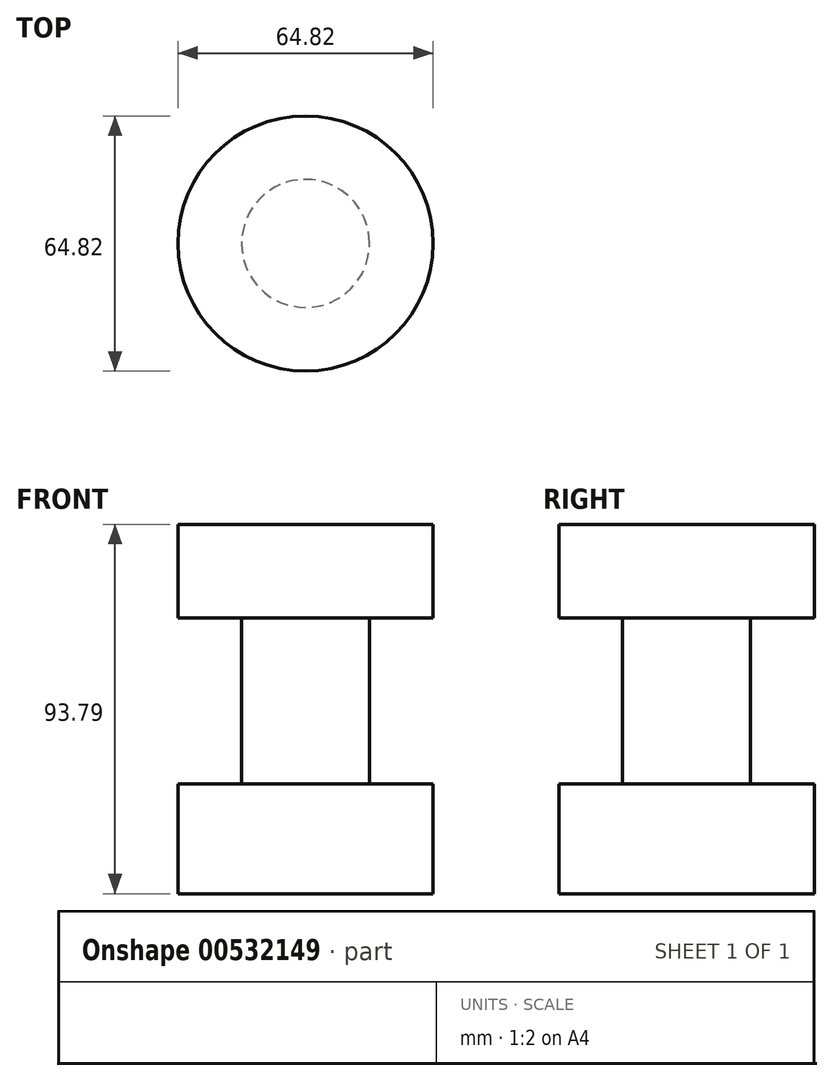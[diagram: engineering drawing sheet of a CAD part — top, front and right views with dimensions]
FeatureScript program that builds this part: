
annotation { "Feature Type Name" : "Feature", "Feature Type Description" : "" }
export const myFeature = defineFeature(function(context is Context, id is Id, definition is map)
    precondition{}
    {
        {
            var Q0;
            Q0=qCreatedBy(makeId("Front.planeOp"),FACE);
            var sketch = newSketch(context, id + "F0", { "sketchPlane" : qUnion([Q0])});
            skLineSegment(sketch, "E0.bottom", {"start": v(0, 0) * mm, "end": v(-32.4, 0) * mm});
            skLineSegment(sketch, "E0.top", {"start": v(0, 93.79) * mm, "end": v(-32.4, 93.79) * mm});
            skLineSegment(sketch, "E0.left", {"start": v(0, 0) * mm, "end": v(0, 93.79) * mm});
            skLineSegment(sketch, "E0.right", {"start": v(-32.4, 0) * mm, "end": v(-32.4, 93.79) * mm});
            skSolve(sketch);
        }
        {
            var Q0;
            Q0 = qSketchRegion(id + "F0", true);
            var Q1;
            Q1=sQuery(id+"F0.wireOp",EDGE,"E0.left");
            revolve(context, id + "F1", {"entities" : qUnion([Q0]), "axis" : qUnion([Q1]), "revolveType" : RevolveType.FULL});
        }
        {
            var Q0;
            Q0=qCreatedBy(makeId("Front.planeOp"),FACE);
            var sketch = newSketch(context, id + "F2", { "sketchPlane" : qUnion([Q0])});
            skLineSegment(sketch, "E1.bottom", {"start": v(-38.69, 70.04) * mm, "end": v(-16.26, 70.04) * mm});
            skLineSegment(sketch, "E1.top", {"start": v(-38.69, 27.94) * mm, "end": v(-16.26, 27.94) * mm});
            skLineSegment(sketch, "E1.left", {"start": v(-38.69, 70.04) * mm, "end": v(-38.69, 27.94) * mm});
            skLineSegment(sketch, "E1.right", {"start": v(-16.26, 70.04) * mm, "end": v(-16.26, 27.94) * mm});
            skLineSegment(sketch, "E2", {"start": v(0, 0) * mm, "end": v(0, 40.53) * mm, "construction": true});
            skSolve(sketch);
        }
        {
            var Q0;
            Q0 = qSketchRegion(id + "F2", true);
            var Q1;
            Q1=sQuery(id+"F2.wireOp",EDGE,"E2");
            revolve(context, id + "F3", {"operationType" : NewBodyOperationType.REMOVE, "entities" : qUnion([Q0]), "axis" : qUnion([Q1]), "revolveType" : RevolveType.FULL, "oppositeDirection" : true});
        }
    });
